# Revit family: TM175_RAYNOR_GARAGE_DOOR
name_source: partatom
category: Doors
units: mm (PartAtom-declared; Revit-internal decimal feet)

## family parameters
Always vertical = Yes
Classification Number = 23.30.10.00
Cut with Voids When Loaded = No
Host = Wall
Room Calculation Point = No
Shared = No

## types (5) — shared parameters
Description = Sectional Insulated Steel Door
Function = Exterior
Height = 0' - 0"
Manufacturer = RAYNOR
Model = TM175
Rough Height = 0' - 0"
Rough Width = 0' - 0"
Thickness = 0' - 0"
URL = https://raynor.com
Wall Closure = By host
Width = 0' - 0"

## per-type parameters (varying)
| type | FULL VERTICAL | HIGH LIFT |
| FULL VERTICAL - LEFT MOTOR | Yes | No |
| FULL VERTICAL - RIGHT MOTOR | Yes | No |
| HIGH LIFT - LEFT MOTOR | No | Yes |
| HIGH LIFT - RIGHT MOTOR | No | Yes |
| NORMAL HEADROOM | No | No |

type visibility flags: 5 boolean params named "<type name>" — each type sets only its own to Yes (folded from table)

## geometry (parser evidence)
native form markers: Sweep x23
no freeform markers — native parametric forms only
